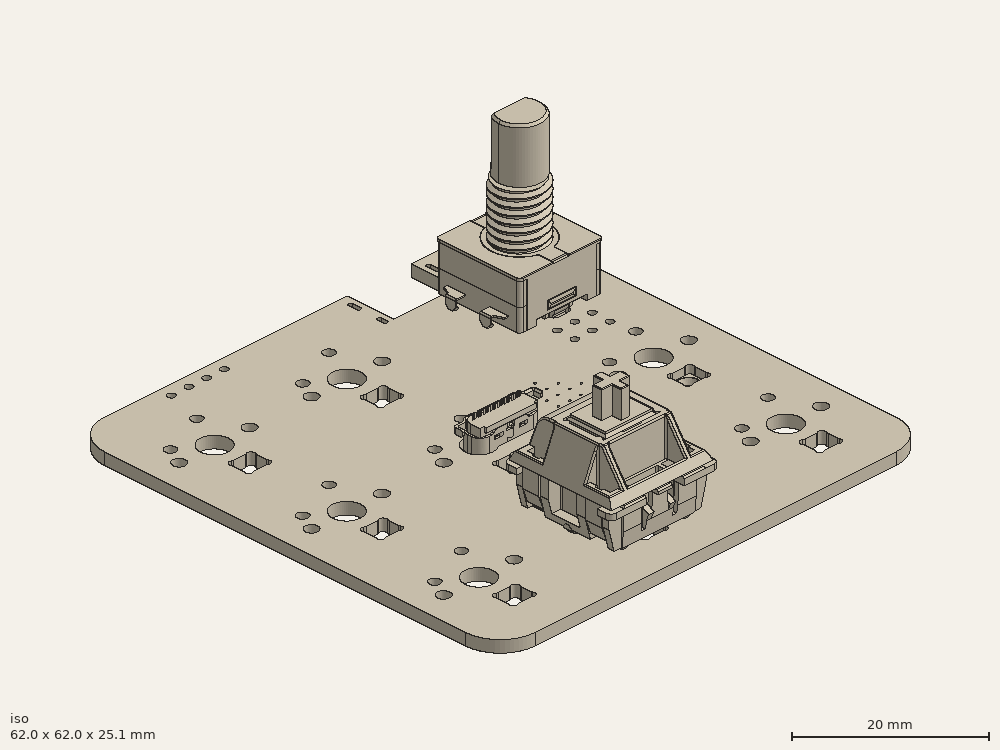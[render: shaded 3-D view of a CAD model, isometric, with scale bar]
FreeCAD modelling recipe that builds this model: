
FCSTD DOCUMENT  (FreeCAD 0.19R24366 (Git))
Label: 1337-freecad
License: All rights reserved
LicenseURL: http://en.wikipedia.org/wiki/All_rights_reserved
objects: App::Link×36, Part::Feature×25, App::Part×6, PartDesign::CoordinateSystem×1, Sketcher::SketchObject×1
note: 27 computed .brp shape members not serialized (recipe doc carries the construction recipe); baked Part::Feature solids carry a one-line shape summary decoded from their .brp

FEATURE [PartDesign::CoordinateSystem] Local_CS_b1b7
  AttacherType = Attacher::AttachEngine3D
FEATURE [Part::Feature] Pcb_b1b7
  Placement = pos=(-104.459,65.3708,0) rot=(0,0,1;0rad)
  shape: bbox 62 x 62 x 1.6 mm, 246 faces (baked)
FEATURE [Sketcher::SketchObject] PCB_Sketch_b1b7
  FullyConstrained = false
  sketch-geometry (9):
    g0: LineSegment StartX=-26 StartY=-31 StartZ=0 EndX=26 EndY=-31 EndZ=0
    g1: LineSegment StartX=26 StartY=31 StartZ=0 EndX=18.175 EndY=31 EndZ=0
    g2: LineSegment StartX=8.935 StartY=31 StartZ=0 EndX=-26 EndY=31 EndZ=0
    g3: LineSegment StartX=-31 StartY=26 StartZ=0 EndX=-31 EndY=-26 EndZ=0
    g4: LineSegment StartX=31 StartY=-26 StartZ=0 EndX=31 EndY=26 EndZ=0
    g5: ArcOfCircle CenterX=-26 CenterY=26 CenterZ=0 NormalX=0 NormalY=0 NormalZ=-1 AngleXU=1.35767e-07 Radius=5 StartAngle=0 EndAngle=1.5708
    g6: ArcOfCircle CenterX=-26 CenterY=-26 CenterZ=0 NormalX=0 NormalY=0 NormalZ=-1 AngleXU=-1.5708 Radius=5 StartAngle=0 EndAngle=1.5708
    g7: ArcOfCircle CenterX=26 CenterY=26 CenterZ=0 NormalX=0 NormalY=0 NormalZ=-1 AngleXU=1.5708 Radius=5 StartAngle=0 EndAngle=1.5708
    g8: ArcOfCircle CenterX=26 CenterY=-26 CenterZ=0 NormalX=0 NormalY=0 NormalZ=-1 AngleXU=-3.14159 Radius=5 StartAngle=0 EndAngle=1.5708
FEATURE [Part::Feature] Shape  label="MX8_SW_Cherry_MX_PCB_cp_10988efbe275"
  Placement = pos=(-3.05375,-19.0187,0) rot=(0,0,1;0rad)
  shape: bbox 15.61 x 15.61 x 18.61 mm, 942 faces, 7 solids (baked)
FEATURE [Part::Feature] Shape001  label="D5_SK6812MINI-E v4_9102173b2550"
  Placement = pos=(22.0963,0.03125,0) rot=(0,0,1;0rad)
  shape: bbox 5.896 x 2.817 x 1.796 mm, 116 faces, 5 solids (baked)
FEATURE [App::Link] MX8_SW_Cherry_MX_PCB_cp_10988efbe275_ln_  label="MX7_SW_Cherry_MX_PCB_cp_2561cabf2a63"
  LinkPlacement = pos=(-22.1037,-19.0187,0) rot=(0,0,1;0rad)
  LinkedObject = -> Shape
  Placement = pos=(-22.1037,-19.0187,0) rot=(0,0,1;0rad)
FEATURE [App::Link] D5_SK6812MINI_E_v4_9102173b2550_ln_  label="D6_SK6812MINI-E v4_df0d764bc56a"
  LinkPlacement = pos=(-22.1037,-19.0187,0) rot=(0,0,1;0rad)
  LinkedObject = -> Shape001
  Placement = pos=(-22.1037,-19.0187,0) rot=(0,0,1;0rad)
FEATURE [App::Link] MX8_SW_Cherry_MX_PCB_cp_10988efbe275_ln_001  label="MX1_SW_Cherry_MX_PCB_cp_098cc94974dd"
  LinkPlacement = pos=(-22.1037,19.0813,0) rot=(0,0,1;0rad)
  LinkedObject = -> Shape
  Placement = pos=(-22.1037,19.0813,0) rot=(0,0,1;0rad)
FEATURE [App::Link] MX8_SW_Cherry_MX_PCB_cp_10988efbe275_ln_002  label="MX6_SW_Cherry_MX_PCB_cp_9e4ca548c5c9"
  LinkPlacement = pos=(22.0963,0.03125,0) rot=(0,0,1;0rad)
  LinkedObject = -> Shape
  Placement = pos=(22.0963,0.03125,0) rot=(0,0,1;0rad)
FEATURE [App::Link] D5_SK6812MINI_E_v4_9102173b2550_ln_001  label="D1_SK6812MINI-E v4_ed1fd5c702c4"
  LinkPlacement = pos=(-22.1037,19.0813,0) rot=(0,0,1;0rad)
  LinkedObject = -> Shape001
  Placement = pos=(-22.1037,19.0813,0) rot=(0,0,1;0rad)
FEATURE [App::Link] MX8_SW_Cherry_MX_PCB_cp_10988efbe275_ln_003  label="MX9_SW_Cherry_MX_PCB_cp_c9ecd395359e"
  LinkPlacement = pos=(22.0963,-19.0187,0) rot=(0,0,1;0rad)
  LinkedObject = -> Shape
  Placement = pos=(22.0963,-19.0187,0) rot=(0,0,1;0rad)
FEATURE [App::Link] MX8_SW_Cherry_MX_PCB_cp_10988efbe275_ln_004  label="MX4_SW_Cherry_MX_PCB_cp_7425710b9109"
  LinkPlacement = pos=(-22.1037,0.03125,0) rot=(0,0,1;0rad)
  LinkedObject = -> Shape
  Placement = pos=(-22.1037,0.03125,0) rot=(0,0,1;0rad)
FEATURE [App::Link] D5_SK6812MINI_E_v4_9102173b2550_ln_002  label="D2_SK6812MINI-E v4_2bb345674183"
  LinkPlacement = pos=(-3.05375,19.0813,0) rot=(0,0,1;0rad)
  LinkedObject = -> Shape001
  Placement = pos=(-3.05375,19.0813,0) rot=(0,0,1;0rad)
FEATURE [Part::Feature] Shape002  label="MX3_ѽת±ძǷ_aba7025db171"
  Placement = pos=(21.8463,19.0813,0) rot=(-0.57735,0.57735,0.57735;4.18879rad)
  shape: bbox 15 x 12.3 x 25.1 mm, 320 faces, 6 solids (baked)
FEATURE [App::Link] D5_SK6812MINI_E_v4_9102173b2550_ln_003  label="D3_SK6812MINI-E v4_80899bd99b1c"
  LinkPlacement = pos=(-22.1037,0.03125,0) rot=(0,0,1;0rad)
  LinkedObject = -> Shape001
  Placement = pos=(-22.1037,0.03125,0) rot=(0,0,1;0rad)
FEATURE [App::Link] D5_SK6812MINI_E_v4_9102173b2550_ln_004  label="D7_SK6812MINI-E v4_e9cb6cc7a03b"
  LinkPlacement = pos=(-3.05375,-19.0187,0) rot=(0,0,1;0rad)
  LinkedObject = -> Shape001
  Placement = pos=(-3.05375,-19.0187,0) rot=(0,0,1;0rad)
FEATURE [App::Link] D5_SK6812MINI_E_v4_9102173b2550_ln_005  label="D8_SK6812MINI-E v4_12ab584928c4"
  LinkPlacement = pos=(22.0963,-19.0187,0) rot=(0,0,1;0rad)
  LinkedObject = -> Shape001
  Placement = pos=(22.0963,-19.0187,0) rot=(0,0,1;0rad)
FEATURE [App::Link] D5_SK6812MINI_E_v4_9102173b2550_ln_006  label="D4_SK6812MINI-E v4_21a97c9b7827"
  LinkPlacement = pos=(-3.05375,0.03125,0) rot=(0,0,1;0rad)
  LinkedObject = -> Shape001
  Placement = pos=(-3.05375,0.03125,0) rot=(0,0,1;0rad)
FEATURE [App::Link] MX8_SW_Cherry_MX_PCB_cp_10988efbe275_ln_005  label="MX2_SW_Cherry_MX_PCB_cp_521c0006c369"
  LinkPlacement = pos=(-3.05375,19.0813,0) rot=(0,0,1;0rad)
  LinkedObject = -> Shape
  Placement = pos=(-3.05375,19.0813,0) rot=(0,0,1;0rad)
FEATURE [App::Link] MX8_SW_Cherry_MX_PCB_cp_10988efbe275_ln_006  label="MX5_SW_Cherry_MX_PCB_cp_448fbf0066d6"
  LinkPlacement = pos=(-3.05375,0.03125,0) rot=(0,0,1;0rad)
  LinkedObject = -> Shape
  Placement = pos=(-3.05375,0.03125,0) rot=(0,0,1;0rad)
FEATURE [App::Part] Top_b1b7
  Group = -> [Shape,Shape001,MX8_SW_Cherry_MX_PCB_cp_10988efbe275_ln_,D5_SK6812MINI_E_v4_9102173b2550_ln_,MX8_SW_Cherry_MX_PCB_cp_10988efbe275_ln_001,MX8_SW_Cherry_MX_PCB_cp_10988efbe275_ln_002,D5_SK6812MINI_E_v4_9102173b2550_ln_001,MX8_SW_Cherry_MX_PCB_cp_10988efbe275_ln_003,MX8_SW_Cherry_MX_PCB_cp_10988efbe275_ln_004,D5_SK6812MINI_E_v4_9102173b2550_ln_002,Shape002,D5_SK6812MINI_E_v4_9102173b2550_ln_003,+5 more]
  Origin = -> Origin003
FEATURE [Part::Feature] Part__Feature  label="SOLID"
  shape: bbox 11.54 x 3.182 x 7.202 mm, 705 faces (baked)
FEATURE [Part::Feature] Part__Feature001  label="COMPOUND"
  shape: bbox 12.24 x 2e-07 x 6.8 mm, 0 faces, 0 solids (baked)
FEATURE [App::Part] _169900001  label="J1_2169900001_644f82124686"
  Group = -> [Part__Feature,Part__Feature001]
  Origin = -> Origin008
  Placement = pos=(13.56,27.425,-1.1) rot=(0,0.707107,-0.707107;3.14159rad)
FEATURE [Part::Feature] Shape003  label="C10_C_0603_1608Metric_47777b6f1f74"
  Placement = pos=(4.515,4.675,-1.6) rot=(0,1,0;3.14159rad)
  shape: bbox 1.6 x 0.8 x 0.8 mm, 28 faces (baked)
FEATURE [App::Link] C10_C_0603_1608Metric_47777b6f1f74_ln_  label="C11_C_0603_1608Metric_b72a783421e1"
  LinkPlacement = pos=(18.445,-1.945,-1.6) rot=(-0.382683,0.92388,0;3.14159rad)
  LinkedObject = -> Shape003
  Placement = pos=(18.445,-1.945,-1.6) rot=(-0.382683,0.92388,0;3.14159rad)
FEATURE [App::Link] C10_C_0603_1608Metric_47777b6f1f74_ln_001  label="C7_C_0603_1608Metric_2723bd853ec4"
  LinkPlacement = pos=(4.515,7.675,-1.6) rot=(0,1,0;3.14159rad)
  LinkedObject = -> Shape003
  Placement = pos=(4.515,7.675,-1.6) rot=(0,1,0;3.14159rad)
FEATURE [Part::Feature] Shape004  label="D9_D_SOD_123F_ec2558b6ef7f"
  Placement = pos=(3.93,24.19,-1.6) rot=(0.707107,-0.707107,0;3.14159rad)
  shape: bbox 1.6 x 3.5 x 1.1 mm, 27 faces (baked)
FEATURE [Part::Feature] Shape005  label="R3_R_0603_1608Metric_703f1d19efee"
  Placement = pos=(12.56,15.22,-1.6) rot=(0.707107,0.707107,0;3.14159rad)
  shape: bbox 0.8 x 1.6 x 0.45 mm, 26 faces (baked)
FEATURE [App::Link] R3_R_0603_1608Metric_703f1d19efee_ln_  label="R2_R_0603_1608Metric_08c6e43905b2"
  LinkPlacement = pos=(9.29,22.855,-1.6) rot=(0.707107,0.707107,0;3.14159rad)
  LinkedObject = -> Shape005
  Placement = pos=(9.29,22.855,-1.6) rot=(0.707107,0.707107,0;3.14159rad)
FEATURE [App::Link] C10_C_0603_1608Metric_47777b6f1f74_ln_002  label="C12_C_0603_1608Metric_d45c730120b2"
  LinkPlacement = pos=(-26.635,-5.025,-1.6) rot=(0.707107,-0.707107,0;3.14159rad)
  LinkedObject = -> Shape003
  Placement = pos=(-26.635,-5.025,-1.6) rot=(0.707107,-0.707107,0;3.14159rad)
FEATURE [App::Link] C10_C_0603_1608Metric_47777b6f1f74_ln_003  label="C6_C_0603_1608Metric_cdd97ceed0a6"
  LinkPlacement = pos=(-26.685,13.975,-1.6) rot=(0.707107,-0.707107,0;3.14159rad)
  LinkedObject = -> Shape003
  Placement = pos=(-26.685,13.975,-1.6) rot=(0.707107,-0.707107,0;3.14159rad)
FEATURE [App::Link] C10_C_0603_1608Metric_47777b6f1f74_ln_004  label="C5_C_0603_1608Metric_883a968ad9f9"
  LinkPlacement = pos=(4.715,16.325,-1.6) rot=(0,1,0;3.14159rad)
  LinkedObject = -> Shape003
  Placement = pos=(4.715,16.325,-1.6) rot=(0,1,0;3.14159rad)
FEATURE [App::Link] R3_R_0603_1608Metric_703f1d19efee_ln_001  label="R4_R_0603_1608Metric_249260675a29"
  LinkPlacement = pos=(11.05,15.22,-1.6) rot=(0.707107,0.707107,0;3.14159rad)
  LinkedObject = -> Shape005
  Placement = pos=(11.05,15.22,-1.6) rot=(0.707107,0.707107,0;3.14159rad)
FEATURE [Part::Feature] Shape006  label="U2_SOT_23_6_ed5257b4cbc5"
  Placement = pos=(11.81,18.8,-1.6) rot=(0.707107,-0.707107,0;3.14159rad)
  shape: bbox 2.9 x 2.8 x 1.55 mm, 124 faces (baked)
FEATURE [Part::Feature] Shape007  label="FB2_L_0603_1608Metric_5ac2a3543efa"
  Placement = pos=(4.7,19.41,-1.6) rot=(1,0,0;3.14159rad)
  shape: bbox 1.6 x 0.8 x 0.8 mm, 28 faces (baked)
FEATURE [Part::Feature] Shape008  label="D13_LED_WS2812B_PLCC4_50x50mm_P32mm_8788541bf0fe"
  Placement = pos=(-12.5787,-9.49375,-1.6) rot=(1,0,0;3.14159rad)
  shape: bbox 5.4 x 5 x 1.6 mm, 68 faces (baked)
FEATURE [App::Link] C10_C_0603_1608Metric_47777b6f1f74_ln_005  label="C13_C_0603_1608Metric_732b4537cc3c"
  LinkPlacement = pos=(12.485,-5.375,-1.6) rot=(0.92388,0.382683,0;3.14159rad)
  LinkedObject = -> Shape003
  Placement = pos=(12.485,-5.375,-1.6) rot=(0.92388,0.382683,0;3.14159rad)
FEATURE [App::Link] FB2_L_0603_1608Metric_5ac2a3543efa_ln_  label="FB1_L_0603_1608Metric_eadd6389cb0a"
  LinkPlacement = pos=(6.475,25.755,-1.6) rot=(0.707107,-0.707107,0;3.14159rad)
  LinkedObject = -> Shape007
  Placement = pos=(6.475,25.755,-1.6) rot=(0.707107,-0.707107,0;3.14159rad)
FEATURE [Part::Feature] Shape009  label="RN1_R_Array_Convex_4x0603_803ffbc19771"
  Placement = pos=(24.7275,19.0813,-1.6) rot=(1,0,0;3.14159rad)
  shape: bbox 1.6 x 3.2 x 0.5 mm, 206 faces (baked)
FEATURE [App::Link] R3_R_0603_1608Metric_703f1d19efee_ln_002  label="R5_R_0603_1608Metric_135521e4561d"
  LinkPlacement = pos=(24.19,13.25,-1.6) rot=(0.707107,0.707107,0;3.14159rad)
  LinkedObject = -> Shape005
  Placement = pos=(24.19,13.25,-1.6) rot=(0.707107,0.707107,0;3.14159rad)
FEATURE [App::Link] C10_C_0603_1608Metric_47777b6f1f74_ln_006  label="C3_C_0603_1608Metric_48b2fe1b6366"
  LinkPlacement = pos=(4.69,17.85,-1.6) rot=(0,1,0;3.14159rad)
  LinkedObject = -> Shape003
  Placement = pos=(4.69,17.85,-1.6) rot=(0,1,0;3.14159rad)
FEATURE [App::Link] R3_R_0603_1608Metric_703f1d19efee_ln_003  label="R6_R_0603_1608Metric_47219c052b4f"
  LinkPlacement = pos=(3.765,2.425,-1.6) rot=(0.707107,-0.707107,0;3.14159rad)
  LinkedObject = -> Shape005
  Placement = pos=(3.765,2.425,-1.6) rot=(0.707107,-0.707107,0;3.14159rad)
FEATURE [App::Link] C10_C_0603_1608Metric_47777b6f1f74_ln_007  label="C8_C_0603_1608Metric_69688f36ee7a"
  LinkPlacement = pos=(4.515,6.175,-1.6) rot=(0,1,0;3.14159rad)
  LinkedObject = -> Shape003
  Placement = pos=(4.515,6.175,-1.6) rot=(0,1,0;3.14159rad)
FEATURE [App::Link] D13_LED_WS2812B_PLCC4_50x50mm_P32mm_8788541bf0fe_ln_  label="D12_LED_WS2812B_PLCC4_50x50mm_P32mm_e819ca6d50cc"
  LinkPlacement = pos=(12.565,-9.49375,-1.6) rot=(1,0,0;3.14159rad)
  LinkedObject = -> Shape008
  Placement = pos=(12.565,-9.49375,-1.6) rot=(1,0,0;3.14159rad)
FEATURE [App::Link] C10_C_0603_1608Metric_47777b6f1f74_ln_008  label="C9_C_0603_1608Metric_451f01d50d0c"
  LinkPlacement = pos=(13.665,5.975,-1.6) rot=(1,0,0;3.14159rad)
  LinkedObject = -> Shape003
  Placement = pos=(13.665,5.975,-1.6) rot=(1,0,0;3.14159rad)
FEATURE [App::Link] C10_C_0603_1608Metric_47777b6f1f74_ln_009  label="C1_C_0603_1608Metric_48ef7e6e8cdd"
  LinkPlacement = pos=(4.69,20.99,-1.6) rot=(1,0,0;3.14159rad)
  LinkedObject = -> Shape003
  Placement = pos=(4.69,20.99,-1.6) rot=(1,0,0;3.14159rad)
FEATURE [Part::Feature] Shape010  label="F1_Fuse_0805_2012Metric_cf59e2bba5d7"
  Placement = pos=(6.81,22.76,-1.6) rot=(0,1,0;3.14159rad)
  shape: bbox 2 x 1.25 x 0.45 mm, 26 faces (baked)
FEATURE [App::Link] D13_LED_WS2812B_PLCC4_50x50mm_P32mm_8788541bf0fe_ln_001  label="D11_LED_WS2812B_PLCC4_50x50mm_P32mm_9dbc2f5811ca"
  LinkPlacement = pos=(-12.5787,9.55625,-1.6) rot=(1,0,0;3.14159rad)
  LinkedObject = -> Shape008
  Placement = pos=(-12.5787,9.55625,-1.6) rot=(1,0,0;3.14159rad)
FEATURE [App::Link] D13_LED_WS2812B_PLCC4_50x50mm_P32mm_8788541bf0fe_ln_002  label="D10_LED_WS2812B_PLCC4_50x50mm_P32mm_920df473fb40"
  LinkPlacement = pos=(12.565,9.575,-1.6) rot=(1,0,0;3.14159rad)
  LinkedObject = -> Shape008
  Placement = pos=(12.565,9.575,-1.6) rot=(1,0,0;3.14159rad)
FEATURE [Part::Feature] Shape011  label="U3_QFN-44-1EP_7x7mm_Pitch0.5mm_53337bc671f7"
  Placement = pos=(9.895,1.56415,-1.6) rot=(-0.382683,0.92388,0;3.14159rad)
  shape: bbox 9.871 x 9.871 x 0.77 mm, 278 faces (baked)
FEATURE [Part::Feature] Shape012  label="Y1_Crystal_SMD_3225-4Pin_3.2x2.5mm_3491f37253a1"
  Placement = pos=(15.455,-3.635,-1.6) rot=(-0.382683,0.92388,0;3.14159rad)
  shape: bbox 3.891 x 3.889 x 0.64 mm, 28 faces (baked)
FEATURE [App::Link] C10_C_0603_1608Metric_47777b6f1f74_ln_010  label="C2_C_0603_1608Metric_906b3a19d50e"
  LinkPlacement = pos=(22.385,20.585,-1.6) rot=(0.707107,0.707107,0;3.14159rad)
  LinkedObject = -> Shape003
  Placement = pos=(22.385,20.585,-1.6) rot=(0.707107,0.707107,0;3.14159rad)
FEATURE [App::Link] C10_C_0603_1608Metric_47777b6f1f74_ln_011  label="C14_C_0603_1608Metric_b648ce40a933"
  LinkPlacement = pos=(-26.685,-24.075,-1.6) rot=(0.707107,-0.707107,0;3.14159rad)
  LinkedObject = -> Shape003
  Placement = pos=(-26.685,-24.075,-1.6) rot=(0.707107,-0.707107,0;3.14159rad)
FEATURE [App::Link] R3_R_0603_1608Metric_703f1d19efee_ln_004  label="R1_R_0603_1608Metric_9f67d3edf26c"
  LinkPlacement = pos=(17.84,22.83,-1.6) rot=(0.707107,-0.707107,0;3.14159rad)
  LinkedObject = -> Shape005
  Placement = pos=(17.84,22.83,-1.6) rot=(0.707107,-0.707107,0;3.14159rad)
FEATURE [Part::Feature] Shape013  label="SW1_SW_SPST_TL3342_e4c693392fab"
  Placement = pos=(9.565,-25.55,-1.6) rot=(0,1,0;3.14159rad)
  shape: bbox 6.401 x 5.201 x 1.541 mm, 193 faces (baked)
FEATURE [App::Link] C10_C_0603_1608Metric_47777b6f1f74_ln_012  label="C4_C_0603_1608Metric_20135b50eba9"
  LinkPlacement = pos=(22.385,17.595,-1.6) rot=(0.707107,-0.707107,0;3.14159rad)
  LinkedObject = -> Shape003
  Placement = pos=(22.385,17.595,-1.6) rot=(0.707107,-0.707107,0;3.14159rad)
FEATURE [App::Part] Bot_b1b7
  Group = -> [_169900001,Shape003,C10_C_0603_1608Metric_47777b6f1f74_ln_,C10_C_0603_1608Metric_47777b6f1f74_ln_001,Shape004,Shape005,R3_R_0603_1608Metric_703f1d19efee_ln_,C10_C_0603_1608Metric_47777b6f1f74_ln_002,C10_C_0603_1608Metric_47777b6f1f74_ln_003,C10_C_0603_1608Metric_47777b6f1f74_ln_004,R3_R_0603_1608Metric_703f1d19efee_ln_001,Shape006,Shape007,Shape008,C10_C_0603_1608Metric_47777b6f1f74_ln_005,+19 more]
  Origin = -> Origin004
FEATURE [App::Part] Step_Models_b1b7
  Group = -> [Top_b1b7,Bot_b1b7]
  Origin = -> Origin002
FEATURE [Part::Feature] topSilks_c99f
  Placement = pos=(-104.459,65.3708,0.07) rot=(0,0,1;0rad)
  shape: bbox 34.44 x 53.22 x 2e-07 mm, 16 faces, 0 solids (baked)
FEATURE [Part::Feature] botSilks_c44b
  Placement = pos=(-104.459,65.3708,-1.67) rot=(0,0,1;0rad)
  shape: bbox 53.6 x 57.6 x 2e-07 mm, 109 faces, 0 solids (baked)
FEATURE [Part::Feature] pads_area016001  label="topPads_b1b7"
  Placement = pos=(-104.459,65.3708,0.02) rot=(0,0,1;0rad)
  shape: bbox 57.51 x 54.65 x 2e-07 mm, 107 faces, 0 solids (baked)
FEATURE [Part::Feature] tracks_area001  label="topTracks_b1b7"
  Placement = pos=(-104.459,65.3708,0.01) rot=(0,0,1;0rad)
  shape: bbox 44.14 x 42.86 x 2e-07 mm, 21 faces, 0 solids (baked)
FEATURE [Part::Feature] zones_area001  label="topZones_b1b7"
  Placement = pos=(-104.459,65.3708,0.01) rot=(0,0,1;0rad)
  shape: bbox 61.55 x 61.55 x 2e-07 mm, 67 faces, 0 solids (baked)
FEATURE [Part::Feature] pads_area016065001  label="botPads_b1b7"
  Placement = pos=(-104.459,65.3708,-1.62) rot=(0,0,1;0rad)
  shape: bbox 57.51 x 58.27 x 2e-07 mm, 259 faces, 0 solids (baked)
FEATURE [Part::Feature] tracks_area002  label="botTracks_b1b7"
  Placement = pos=(-104.459,65.3708,-1.61) rot=(0,0,1;0rad)
  shape: bbox 57.57 x 58.37 x 2e-07 mm, 67 faces, 0 solids (baked)
FEATURE [Part::Feature] zones_area002  label="botZones_b1b7"
  Placement = pos=(-104.459,65.3708,-1.61) rot=(0,0,1;0rad)
  shape: bbox 61.55 x 61.55 x 2e-07 mm, 162 faces, 0 solids (baked)
FEATURE [App::Part] Board_Geoms_b1b7
  Group = -> [Local_CS_b1b7,Pcb_b1b7,PCB_Sketch_b1b7,topSilks_c99f,botSilks_c44b,pads_area016001,tracks_area001,zones_area001,pads_area016065001,tracks_area002,zones_area002]
  Origin = -> Origin
FEATURE [App::Part] Board_b1b7  label="1337-v4.0"
  Group = -> [Board_Geoms_b1b7,Step_Models_b1b7]
  Origin = -> Origin001
